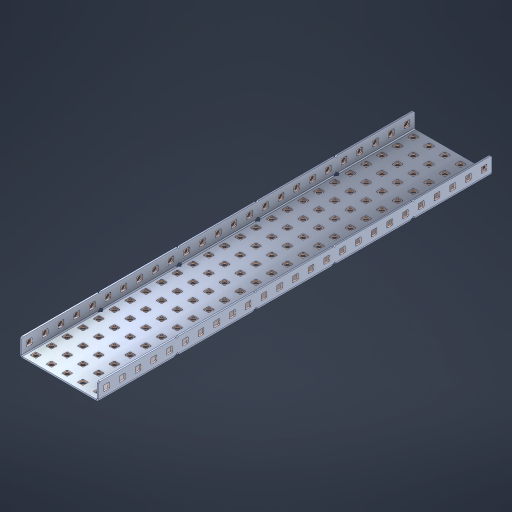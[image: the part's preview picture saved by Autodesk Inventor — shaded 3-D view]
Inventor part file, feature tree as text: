
AUTODESK INVENTOR PART (.ipt)
format: ipt  version: 2023 (Build 270158000, 158)  size: 1,935,872 bytes
history: native  units: in
note: dims shown in document units (in); Inventor stores cm internally (conversion verified against a paired STEP export)
features: other x180, extrude x174, sheet_metal_op x10, sketch x8, mirror x1, pattern_linear x1, chamfer x1
ambient origin geometry x8: Origin, YZ Plane, XZ Plane, XY Plane, X Axis, Y Axis, Z Axis, Center Point
bodies: Solid1 (feature_tree), Body (feature_tree)
feature tree (375):
  other  "Flange Pattern Plane"
  sheet_metal_op  "Flange Pattern"
  sheet_metal_op  "Body Pattern"
  other  "Arc Length"
  mirror  "Notch Mirror"
  pattern_linear  "Notch Pattern"  Spacing1=0.1875in  [1 undecoded]
  chamfer  "End Chamfer"
  extrude  "Half Cut"  Depth=0.0469in
  sketch  "Sketch1"  dims[d0=2.5in]
  other  "Plate1"
  sketch  "Sketch2"  dims[d1=12.5in]
  other  "Plate2"
  sheet_metal_op  "Bend1"
  sheet_metal_op  "Corner1"
  sketch  "Sketch3"  dims[d2=0.0469in]
  other  "Flange Pattern Sketch"
  sketch  "Sketch7"  dims[d3=0.0469in]
  other  "Srf1"
  other  "Srf2"
  sketch  "Sketch8"  dims[d4=0.0234in]
  sketch  "Sketch9"  dims[d5=0.0938in]
  other  "Srf91"
  sheet_metal_op  "Body Pattern Sketch"
  other  "Srf92"
  sketch  "Sketch13"  dims[d6=0.0469in]
  sketch  "Sketch14"  dims[d7=0.5in d8=90.0deg d9=0.0312in d10=0.1875in d11=0.0469in d12=0.0469in d16=0.182in d17=0.02in d18=0.0469in d19=0.0in d20=0.25in d21=0.25in d46=0.172in d47=1.0in d48=0.0in d49=0.182in d50=0.02in d51=0.25in d52=0.25in d53=0.0469in d54=0.0in d55=0.172in d56=1.0in d57=0.0in d60=9.8425in d62=0.5in d63=1.9685in d65=0.5in d85=0.1227in d86=0.1659in d88=0.04in d89=0.0469in d90=0.0in d91=0.04in d92=0.0491in d95=2.5in d96=0.04in d97=0.25in d98=45.0deg d101=0.0in d102=2.497in d131=2.5in d132=9.8425in d134=0.5in d139=0.5in]
  other  "Srf856"
  other  "Srf1310"
  other  "Srf1311"
  other  "Srf1312"
  other  "Srf1376"
  other  "Srf1377"
  other  "Srf1728"
  other  "Srf1755"
  other  "Srf1878"
  other  "Srf1879"
  other  "Srf1880"
  other  "Srf1881"
  other  "Srf1882"
  other  "Srf1883"
  other  "Srf1884"
  other  "Srf1885"
  other  "Srf1886"
  other  "Srf1887"
  other  "Srf1888"
  other  "Srf1889"
  other  "Srf1890"
  other  "Srf1891"
  other  "Srf1892"
  other  "Srf1893"
  other  "Srf1894"
  other  "Srf1895"
  other  "Srf1896"
  other  "Srf1897"
  other  "Srf1898"
  other  "Srf1899"
  other  "Srf1900"
  other  "Srf1901"
  other  "Srf1902"
  other  "Srf1903"
  other  "Srf1904"
  other  "Srf1905"
  other  "Srf1906"
  other  "Srf1942"
  other  "Srf1943"
  other  "Srf1944"
  other  "Srf1945"
  other  "Srf1946"
  other  "Srf1947"
  other  "Srf1948"
  other  "Srf1949"
  other  "Srf1950"
  other  "Srf1951"
  other  "Srf1952"
  other  "Srf1953"
  other  "Srf1954"
  other  "Srf1955"
  other  "Srf1956"
  other  "Srf1957"
  other  "Srf1958"
  other  "Srf1959"
  other  "Srf1960"
  other  "Srf1961"
  other  "Srf1962"
  other  "Srf1963"
  other  "Srf1964"
  other  "Srf1965"
  other  "Srf1966"
  other  "Srf1967"
  other  "Srf1968"
  other  "Srf1969"
  other  "Srf1970"
  other  "Srf2111"
  other  "Srf2112"
  other  "Srf2113"
  other  "Srf2114"
  other  "Srf2115"
  other  "Srf2116"
  other  "Srf2117"
  other  "Srf2118"
  other  "Srf2119"
  other  "Srf2120"
  other  "Srf2121"
  other  "Srf2122"
  other  "Srf2123"
  other  "Srf2124"
  other  "Srf2125"
  other  "Srf2146"
  other  "Srf2147"
  other  "Srf2148"
  other  "Srf2149"
  other  "Srf2150"
  other  "Srf2151"
  other  "Srf2152"
  other  "Srf2153"
  other  "Srf2154"
  other  "Srf2155"
  other  "Srf2156"
  other  "Srf2157"
  other  "Srf2158"
  other  "Srf2159"
  other  "Srf2160"
  other  "Srf2161"
  other  "Srf2162"
  other  "Srf2163"
  other  "Srf2164"
  other  "Srf2165"
  other  "Srf2166"
  other  "Srf2167"
  other  "Srf2168"
  other  "Srf2169"
  other  "Srf2170"
  other  "Srf2171"
  other  "Srf2172"
  other  "Srf2173"
  other  "Srf2174"
  other  "Srf2175"
  other  "Srf2176"
  other  "Srf2177"
  other  "Srf2178"
  other  "Srf2179"
  other  "Srf2180"
  other  "Srf2181"
  other  "Srf2182"
  other  "Srf2183"
  other  "Srf2184"
  other  "Srf2185"
  other  "Srf2186"
  other  "Srf2187"
  other  "Srf2188"
  other  "Srf2189"
  other  "Srf2190"
  other  "Srf2191"
  other  "Srf2192"
  other  "Srf2193"
  other  "Srf2194"
  other  "Srf2195"
  other  "Srf2196"
  other  "Srf2197"
  other  "Srf2198"
  other  "Srf2199"
  other  "Srf2200"
  other  "Srf2201"
  other  "Srf2202"
  other  "Srf2203"
  other  "Srf2204"
  other  "Srf2205"
  other  "Srf2206"
  other  "Srf2207"
  other  "Srf2208"
  other  "Srf2209"
  other  "Srf2210"
  other  "Srf2211"
  other  "Srf2212"
  other  "Srf2213"
  other  "Srf2214"
  other  "Srf2215"
  other  "Srf2216"
  other  "Srf2217"
  other  "Srf2218"
  other  "Srf2219"
  other  "Srf2220"
  other  "Srf2221"
  other  "Srf2222"
  other  "Srf2223"
  other  "Srf2224"
  other  "Srf2225"
  other  "Srf2226"
  other  "Srf2227"
  other  "Srf2228"
  other  "Srf2229"
  other  "Srf2230"
  other  "Srf2231"
  other  "Srf2232"
  other  "Srf2233"
  other  "Srf2234"
  other  "Srf2235"
  sheet_metal_op  "Flange Stamp"
  sheet_metal_op  "Flange Circle"
  sheet_metal_op  "Body Stamp"
  sheet_metal_op  "Body Circle"
  sheet_metal_op  "Notch"
  extrude  "ExtrusionSrf2"  Depth=0.0469in
  extrude  "ExtrusionSrf92"  Depth=2.5in
  extrude  "ExtrusionSrf856"  Depth=0.02in
  extrude  "ExtrusionSrf1310"  Depth=0.0469in
  extrude  "ExtrusionSrf1311"  TaperAngle=0.0deg  [1 undecoded]
  extrude  "ExtrusionSrf1312"  Depth=0.25in
  extrude  "ExtrusionSrf1376"  Depth=0.25in
  extrude  "ExtrusionSrf1377"  Depth=2.5in
  extrude  "ExtrusionSrf1728"  Depth=2.5in TaperAngle=0.0deg
  extrude  "ExtrusionSrf1755"  Depth=2.5in
  extrude  "ExtrusionSrf1878"  Depth=0.02in
  extrude  "ExtrusionSrf1879"  Depth=0.25in
  extrude  "ExtrusionSrf1880"  Depth=0.25in
  extrude  "ExtrusionSrf1881"  Depth=0.0469in
  extrude  "ExtrusionSrf1882"  TaperAngle=0.0deg  [1 undecoded]
  extrude  "ExtrusionSrf1883"  Depth=2.5in
  extrude  "ExtrusionSrf1884"  Depth=2.5in TaperAngle=0.0deg
  extrude  "ExtrusionSrf1885"  Depth=2.5in
  extrude  "ExtrusionSrf1886"  Depth=2.5in
  extrude  "ExtrusionSrf1887"  Depth=2.5in
  extrude  "ExtrusionSrf1888"  Depth=2.5in
  extrude  "ExtrusionSrf1889"  Depth=2.5in
  extrude  "ExtrusionSrf1890"  Depth=0.0469in
  extrude  "ExtrusionSrf1891"  TaperAngle=0.0deg  [1 undecoded]
  extrude  "ExtrusionSrf1892"  Depth=2.5in
  extrude  "ExtrusionSrf1893"  Depth=2.5in
  extrude  "ExtrusionSrf1894"  Depth=2.5in
  extrude  "ExtrusionSrf1895"  Depth=0.25in TaperAngle=45.0deg
  extrude  "ExtrusionSrf1896"  TaperAngle=0.0deg  [1 undecoded]
  extrude  "ExtrusionSrf1897"  Depth=2.5in
  extrude  "ExtrusionSrf1898"  Depth=2.5in
  extrude  "ExtrusionSrf1899"  Depth=2.5in
  extrude  "ExtrusionSrf1900"  Depth=2.5in
  extrude  "ExtrusionSrf1901"  Depth=2.5in
  extrude  "ExtrusionSrf1902"  [1 undecoded]
  extrude  "ExtrusionSrf1903"  [1 undecoded]
  extrude  "ExtrusionSrf1904"  [1 undecoded]
  extrude  "ExtrusionSrf1905"  [1 undecoded]
  extrude  "ExtrusionSrf1906"  [1 undecoded]
  extrude  "ExtrusionSrf1942"  [1 undecoded]
  extrude  "ExtrusionSrf1943"  [1 undecoded]
  extrude  "ExtrusionSrf1944"  [1 undecoded]
  extrude  "ExtrusionSrf1945"  [1 undecoded]
  extrude  "ExtrusionSrf1946"  [1 undecoded]
  extrude  "ExtrusionSrf1947"  [1 undecoded]
  extrude  "ExtrusionSrf1948"  [1 undecoded]
  extrude  "ExtrusionSrf1949"  [1 undecoded]
  extrude  "ExtrusionSrf1950"  [1 undecoded]
  extrude  "ExtrusionSrf1951"  [1 undecoded]
  extrude  "ExtrusionSrf1952"  [1 undecoded]
  extrude  "ExtrusionSrf1953"  [1 undecoded]
  extrude  "ExtrusionSrf1954"  [1 undecoded]
  extrude  "ExtrusionSrf1955"  [1 undecoded]
  extrude  "ExtrusionSrf1956"  [1 undecoded]
  extrude  "ExtrusionSrf1957"  [1 undecoded]
  extrude  "ExtrusionSrf1958"  [1 undecoded]
  extrude  "ExtrusionSrf1959"  [1 undecoded]
  extrude  "ExtrusionSrf1960"  [1 undecoded]
  extrude  "ExtrusionSrf1961"  [1 undecoded]
  extrude  "ExtrusionSrf1962"  [1 undecoded]
  extrude  "ExtrusionSrf1963"  [1 undecoded]
  extrude  "ExtrusionSrf1964"  [1 undecoded]
  extrude  "ExtrusionSrf1965"  [1 undecoded]
  extrude  "ExtrusionSrf1966"  [1 undecoded]
  extrude  "ExtrusionSrf1967"  [1 undecoded]
  extrude  "ExtrusionSrf1968"  [1 undecoded]
  extrude  "ExtrusionSrf1969"  [1 undecoded]
  extrude  "ExtrusionSrf1970"  [1 undecoded]
  extrude  "ExtrusionSrf2111"  [1 undecoded]
  extrude  "ExtrusionSrf2112"  [1 undecoded]
  extrude  "ExtrusionSrf2113"  [1 undecoded]
  extrude  "ExtrusionSrf2114"  [1 undecoded]
  extrude  "ExtrusionSrf2115"  [1 undecoded]
  extrude  "ExtrusionSrf2116"  [1 undecoded]
  extrude  "ExtrusionSrf2117"  [1 undecoded]
  extrude  "ExtrusionSrf2118"  [1 undecoded]
  extrude  "ExtrusionSrf2119"  [1 undecoded]
  extrude  "ExtrusionSrf2120"  [1 undecoded]
  extrude  "ExtrusionSrf2121"  [1 undecoded]
  extrude  "ExtrusionSrf2122"  [1 undecoded]
  extrude  "ExtrusionSrf2123"  [1 undecoded]
  extrude  "ExtrusionSrf2124"  [1 undecoded]
  extrude  "ExtrusionSrf2125"  [1 undecoded]
  extrude  "ExtrusionSrf2146"  [1 undecoded]
  extrude  "ExtrusionSrf2147"  [1 undecoded]
  extrude  "ExtrusionSrf2148"  [1 undecoded]
  extrude  "ExtrusionSrf2149"  [1 undecoded]
  extrude  "ExtrusionSrf2150"  [1 undecoded]
  extrude  "ExtrusionSrf2151"  [1 undecoded]
  extrude  "ExtrusionSrf2152"  [1 undecoded]
  extrude  "ExtrusionSrf2153"  [1 undecoded]
  extrude  "ExtrusionSrf2154"  [1 undecoded]
  extrude  "ExtrusionSrf2155"  [1 undecoded]
  extrude  "ExtrusionSrf2156"  [1 undecoded]
  extrude  "ExtrusionSrf2157"  [1 undecoded]
  extrude  "ExtrusionSrf2158"  [1 undecoded]
  extrude  "ExtrusionSrf2159"  [1 undecoded]
  extrude  "ExtrusionSrf2160"  [1 undecoded]
  extrude  "ExtrusionSrf2161"  [1 undecoded]
  extrude  "ExtrusionSrf2162"  [1 undecoded]
  extrude  "ExtrusionSrf2163"  [1 undecoded]
  extrude  "ExtrusionSrf2164"  [1 undecoded]
  extrude  "ExtrusionSrf2165"  [1 undecoded]
  extrude  "ExtrusionSrf2166"  [1 undecoded]
  extrude  "ExtrusionSrf2167"  [1 undecoded]
  extrude  "ExtrusionSrf2168"  [1 undecoded]
  extrude  "ExtrusionSrf2169"  [1 undecoded]
  extrude  "ExtrusionSrf2170"  [1 undecoded]
  extrude  "ExtrusionSrf2171"  [1 undecoded]
  extrude  "ExtrusionSrf2172"  [1 undecoded]
  extrude  "ExtrusionSrf2173"  [1 undecoded]
  extrude  "ExtrusionSrf2174"  [1 undecoded]
  extrude  "ExtrusionSrf2175"  [1 undecoded]
  extrude  "ExtrusionSrf2176"  [1 undecoded]
  extrude  "ExtrusionSrf2177"  [1 undecoded]
  extrude  "ExtrusionSrf2178"  [1 undecoded]
  extrude  "ExtrusionSrf2179"  [1 undecoded]
  extrude  "ExtrusionSrf2180"  [1 undecoded]
  extrude  "ExtrusionSrf2181"  [1 undecoded]
  extrude  "ExtrusionSrf2182"  [1 undecoded]
  extrude  "ExtrusionSrf2183"  [1 undecoded]
  extrude  "ExtrusionSrf2184"  [1 undecoded]
  extrude  "ExtrusionSrf2185"  [1 undecoded]
  extrude  "ExtrusionSrf2186"  [1 undecoded]
  extrude  "ExtrusionSrf2187"  [1 undecoded]
  extrude  "ExtrusionSrf2188"  [1 undecoded]
  extrude  "ExtrusionSrf2189"  [1 undecoded]
  extrude  "ExtrusionSrf2190"  [1 undecoded]
  extrude  "ExtrusionSrf2191"  [1 undecoded]
  extrude  "ExtrusionSrf2192"  [1 undecoded]
  extrude  "ExtrusionSrf2193"  [1 undecoded]
  extrude  "ExtrusionSrf2194"  [1 undecoded]
  extrude  "ExtrusionSrf2195"  [1 undecoded]
  extrude  "ExtrusionSrf2196"  [1 undecoded]
  extrude  "ExtrusionSrf2197"  [1 undecoded]
  extrude  "ExtrusionSrf2198"  [1 undecoded]
  extrude  "ExtrusionSrf2199"  [1 undecoded]
  extrude  "ExtrusionSrf2200"  [1 undecoded]
  extrude  "ExtrusionSrf2201"  [1 undecoded]
  extrude  "ExtrusionSrf2202"  [1 undecoded]
  extrude  "ExtrusionSrf2203"  [1 undecoded]
  extrude  "ExtrusionSrf2204"  [1 undecoded]
  extrude  "ExtrusionSrf2205"  [1 undecoded]
  extrude  "ExtrusionSrf2206"  [1 undecoded]
  extrude  "ExtrusionSrf2207"  [1 undecoded]
  extrude  "ExtrusionSrf2208"  [1 undecoded]
  extrude  "ExtrusionSrf2209"  [1 undecoded]
  extrude  "ExtrusionSrf2210"  [1 undecoded]
  extrude  "ExtrusionSrf2211"  [1 undecoded]
  extrude  "ExtrusionSrf2212"  [1 undecoded]
  extrude  "ExtrusionSrf2213"  [1 undecoded]
  extrude  "ExtrusionSrf2214"  [1 undecoded]
  extrude  "ExtrusionSrf2215"  [1 undecoded]
  extrude  "ExtrusionSrf2216"  [1 undecoded]
  extrude  "ExtrusionSrf2217"  [1 undecoded]
  extrude  "ExtrusionSrf2218"  [1 undecoded]
  extrude  "ExtrusionSrf2219"  [1 undecoded]
  extrude  "ExtrusionSrf2220"  [1 undecoded]
  extrude  "ExtrusionSrf2221"  [1 undecoded]
  extrude  "ExtrusionSrf2222"  [1 undecoded]
  extrude  "ExtrusionSrf2223"  [1 undecoded]
  extrude  "ExtrusionSrf2224"  [1 undecoded]
  extrude  "ExtrusionSrf2225"  [1 undecoded]
  extrude  "ExtrusionSrf2226"  [1 undecoded]
  extrude  "ExtrusionSrf2227"  [1 undecoded]
  extrude  "ExtrusionSrf2228"  [1 undecoded]
  extrude  "ExtrusionSrf2229"  [1 undecoded]
  extrude  "ExtrusionSrf2230"  [1 undecoded]
  extrude  "ExtrusionSrf2231"  [1 undecoded]
  extrude  "ExtrusionSrf2232"  [1 undecoded]
  extrude  "ExtrusionSrf2233"  [1 undecoded]
  extrude  "ExtrusionSrf2234"  [1 undecoded]
  extrude  "ExtrusionSrf2235"  [1 undecoded]
note: 144 required parameter values undecoded (feature->parameter linkage not recoverable at this tier; creation-order binding heuristic only, values carry confidence <= 0.55)
